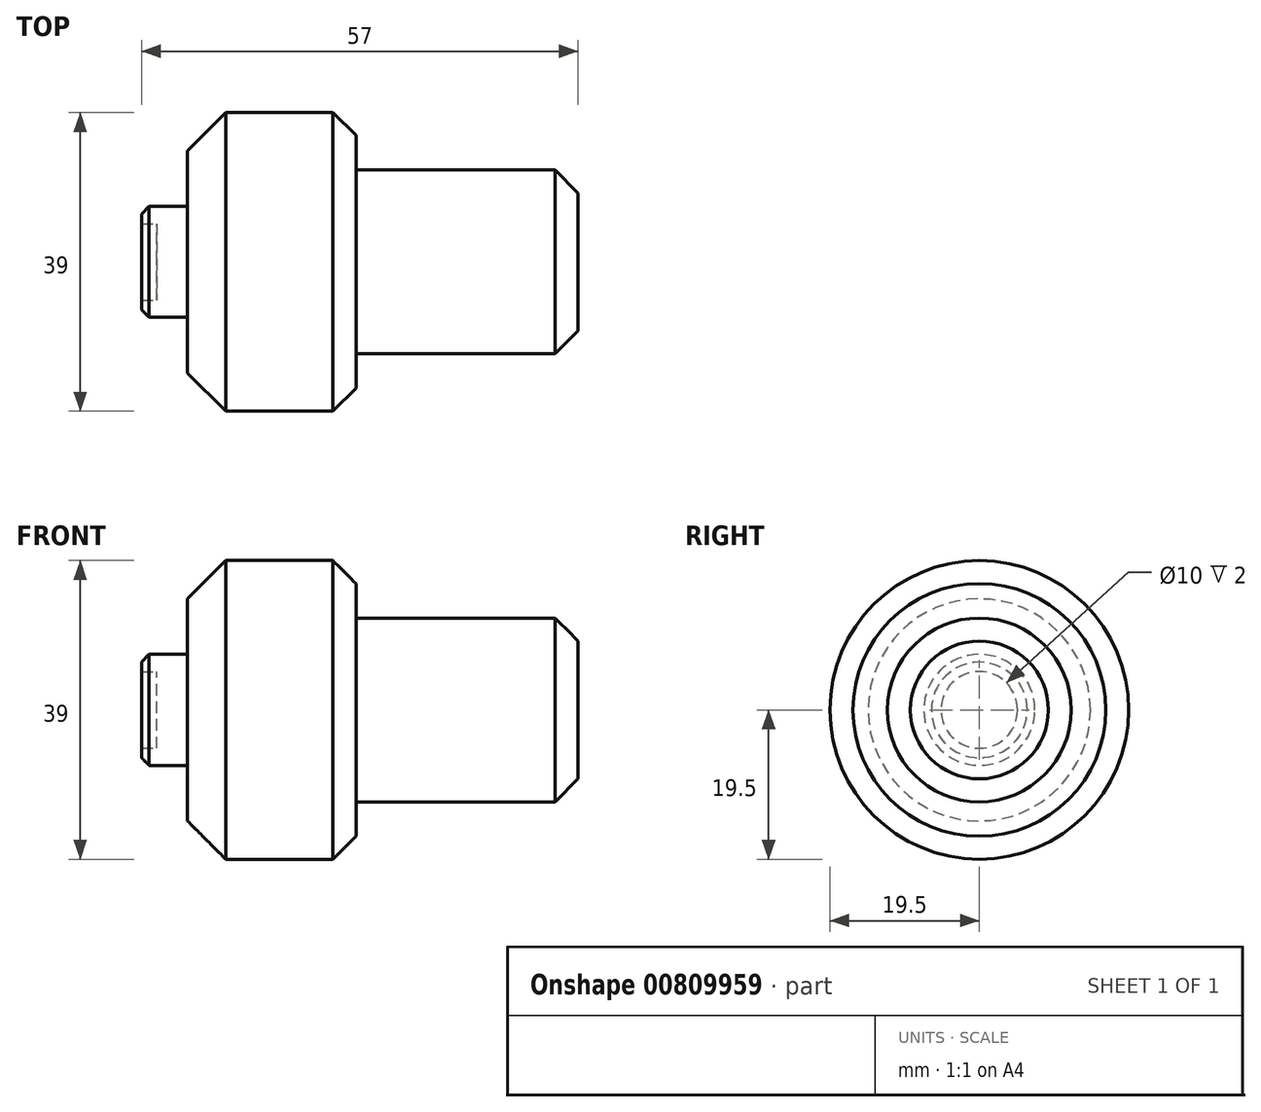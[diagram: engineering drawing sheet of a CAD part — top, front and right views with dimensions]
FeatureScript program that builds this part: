
annotation { "Feature Type Name" : "Feature", "Feature Type Description" : "" }
export const myFeature = defineFeature(function(context is Context, id is Id, definition is map)
    precondition{}
    {
        {
            var Q0;
            Q0=qCreatedBy(makeId("Front.planeOp"),FACE);
            var sketch = newSketch(context, id + "F0", { "sketchPlane" : qUnion([Q0])});
            skLineSegment(sketch, "E0", {"start": v(0, 0) * mm, "end": v(0, 5) * mm});
            skLineSegment(sketch, "E1", {"start": v(0, 5) * mm, "end": v(-2, 5) * mm});
            skLineSegment(sketch, "E2", {"start": v(-2, 5) * mm, "end": v(-2, 7.25) * mm});
            skLineSegment(sketch, "E3", {"start": v(-2, 7.25) * mm, "end": v(4, 7.25) * mm});
            skLineSegment(sketch, "E4", {"start": v(4, 7.25) * mm, "end": v(4, 19.5) * mm});
            skLineSegment(sketch, "E5", {"start": v(4, 19.5) * mm, "end": v(26, 19.5) * mm});
            skLineSegment(sketch, "E6", {"start": v(26, 19.5) * mm, "end": v(26, 12) * mm});
            skLineSegment(sketch, "E7", {"start": v(26, 12) * mm, "end": v(55, 12) * mm});
            skLineSegment(sketch, "E8", {"start": v(55, 12) * mm, "end": v(55, 0) * mm});
            skLineSegment(sketch, "E9", {"start": v(55, 0) * mm, "end": v(0, 0) * mm});
            skSolve(sketch);
        }
        {
            var Q0;
            Q0=makeQuery(id+"F0.imprint","IMPRINT",FACE,{"disambiguationData":[TD([[makeQuery(id+"F0.imprint","IMPRINT",EDGE,{"derivedFrom":sQuery(id+"F0.wireOp",EDGE,"E0")}),-1.0]])]});
            var Q1;
            Q1=sQuery(id+"F0.wireOp",EDGE,"E9");
            revolve(context, id + "F1", {"surfaceOperationType" : NewSurfaceOperationType.NEW, "entities" : qUnion([Q0]), "axis" : qUnion([Q1]), "revolveType" : RevolveType.FULL});
        }
        {
            var Q0;
            Q0=makeQuery(id+"F1.opRevolve","SWEPT_EDGE",EDGE,{"disambiguationData":[OSD([sQuery(id+"F0.wireOp",EDGE,"E4"),sQuery(id+"F0.wireOp",EDGE,"E5")])]});
            chamfer(context, id + "F2", {"entities" : qUnion([Q0]), "width" : 5 * mm, "tangentPropagation" : true});
        }
        {
            var Q0;
            Q0=makeQuery(id+"F1.opRevolve","SWEPT_EDGE",EDGE,{"disambiguationData":[OSD([sQuery(id+"F0.wireOp",EDGE,"E5"),sQuery(id+"F0.wireOp",EDGE,"E6")])]});
            var Q1;
            Q1=makeQuery(id+"F1.opRevolve","SWEPT_EDGE",EDGE,{"disambiguationData":[OSD([sQuery(id+"F0.wireOp",EDGE,"E7"),sQuery(id+"F0.wireOp",EDGE,"E8")])]});
            chamfer(context, id + "F3", {"entities" : qUnion([Q0, Q1]), "width" : 3 * mm, "tangentPropagation" : true});
        }
        {
            var Q0;
            Q0=makeQuery(id+"F1.opRevolve","SWEPT_EDGE",EDGE,{"disambiguationData":[OSD([sQuery(id+"F0.wireOp",EDGE,"E2"),sQuery(id+"F0.wireOp",EDGE,"E3")])]});
            chamfer(context, id + "F4", {"entities" : qUnion([Q0]), "width" : 1 * mm, "tangentPropagation" : true});
        }
    });
